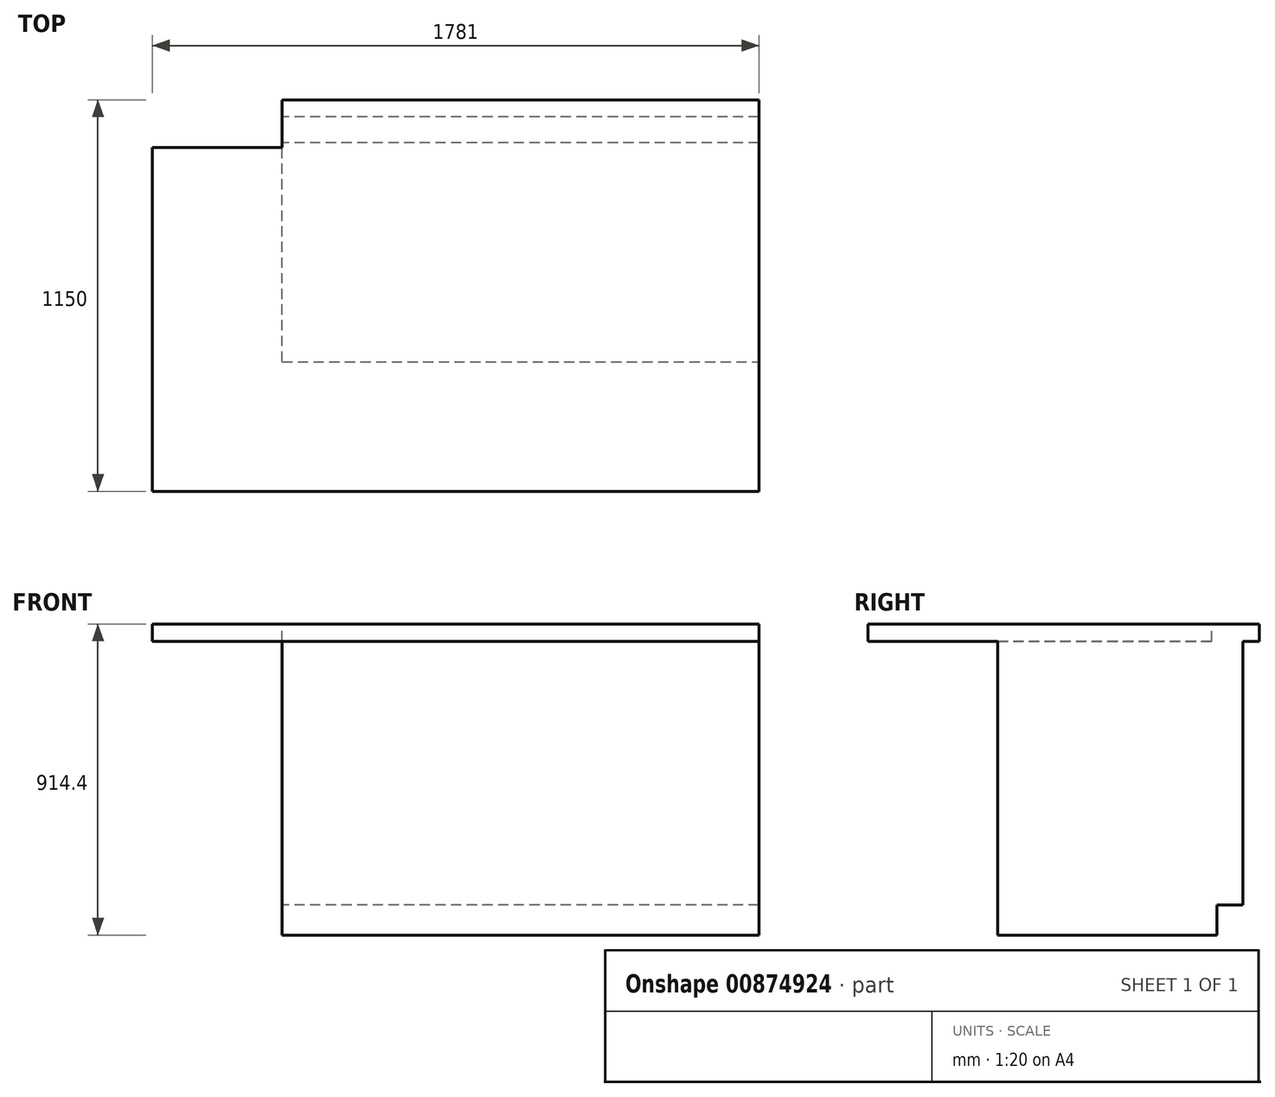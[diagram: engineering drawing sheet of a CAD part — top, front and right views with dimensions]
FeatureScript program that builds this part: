
annotation { "Feature Type Name" : "Feature", "Feature Type Description" : "" }
export const myFeature = defineFeature(function(context is Context, id is Id, definition is map)
    precondition{}
    {
        {
            var Q0;
            Q0=qCreatedBy(makeId("Top.planeOp"),FACE);
            var sketch = newSketch(context, id + "F0", { "sketchPlane" : qUnion([Q0])});
            skLineSegment(sketch, "E0.bottom", {"start": v(0, 0) * mm, "end": v(1400, 0) * mm});
            skLineSegment(sketch, "E0.top", {"start": v(0, 720) * mm, "end": v(1400, 720) * mm});
            skLineSegment(sketch, "E0.left", {"start": v(0, 0) * mm, "end": v(0, 720) * mm});
            skLineSegment(sketch, "E0.right", {"start": v(1400, 0) * mm, "end": v(1400, 720) * mm});
            skSolve(sketch);
        }
        {
            var Q0;
            Q0=makeQuery(id+"F0.imprint","IMPRINT",FACE,{"disambiguationData":[TD([[makeQuery(id+"F0.imprint","IMPRINT",EDGE,{"derivedFrom":sQuery(id+"F0.wireOp",EDGE,"E0.bottom")}),1.0]])]});
            extrude(context, id + "F1", {"entities" : qUnion([Q0]), "depth" : 863.6 * mm, "offsetDistance" : 25 * mm});
        }
        {
            var Q0;
            Q0=qCreatedBy(makeId("Right.planeOp"),FACE);
            var sketch = newSketch(context, id + "F2", { "sketchPlane" : qUnion([Q0])});
            skLineSegment(sketch, "E1.0", {"start": v(0, 0) * mm, "end": v(720, 0) * mm, "construction": true});
            skLineSegment(sketch, "E2.0", {"start": v(720, 863.6) * mm, "end": v(720, 0) * mm, "construction": true});
            skLineSegment(sketch, "E3.0", {"start": v(0, 863.6) * mm, "end": v(0, 0) * mm, "construction": true});
            skLineSegment(sketch, "E4.bottom", {"start": v(720, 0) * mm, "end": v(643.8, 0) * mm});
            skLineSegment(sketch, "E4.top", {"start": v(720, 88.9) * mm, "end": v(643.8, 88.9) * mm});
            skLineSegment(sketch, "E4.left", {"start": v(720, 0) * mm, "end": v(720, 88.9) * mm});
            skLineSegment(sketch, "E4.right", {"start": v(643.8, 0) * mm, "end": v(643.8, 88.9) * mm});
            skSolve(sketch);
        }
        {
            var Q0;
            Q0=qSketchRegion(id+"F2",true);
            extrude(context, id + "F3", {"entities" : qUnion([Q0]), "operationType" : NewBodyOperationType.REMOVE, "endBound" : BoundingType.THROUGH_ALL, "depth" : 25 * mm, "offsetDistance" : 25 * mm});
        }
        {
            var Q0;
            Q0=qCreatedBy(makeId("Right.planeOp"),FACE);
            var sketch = newSketch(context, id + "F4", { "sketchPlane" : qUnion([Q0])});
            skLineSegment(sketch, "E5.0", {"start": v(0, 863.6) * mm, "end": v(720, 863.6) * mm, "construction": true});
            skLineSegment(sketch, "E6.bottom", {"start": v(769, 863.6) * mm, "end": v(-381, 863.6) * mm});
            skLineSegment(sketch, "E6.top", {"start": v(769, 914.4) * mm, "end": v(-381, 914.4) * mm});
            skLineSegment(sketch, "E6.left", {"start": v(769, 863.6) * mm, "end": v(769, 914.4) * mm});
            skLineSegment(sketch, "E6.right", {"start": v(-381, 863.6) * mm, "end": v(-381, 914.4) * mm});
            skSolve(sketch);
        }
        {
            var Q0;
            Q0=makeQuery(id+"F4.imprint","IMPRINT",FACE,{"disambiguationData":[TD([[makeQuery(id+"F4.imprint","IMPRINT",EDGE,{"derivedFrom":sQuery(id+"F4.wireOp",EDGE,"E6.bottom")}),-1.0]])]});
            var Q1;
            Q1=makeQuery(id+"F1.opExtrude","SWEPT_FACE",FACE,{"disambiguationData":[OSD([sQuery(id+"F0.wireOp",EDGE,"E0.right")])]});
            extrude(context, id + "F5", {"entities" : qUnion([Q0]), "endBound" : BoundingType.UP_TO_SURFACE, "depth" : 25 * mm, "endBoundEntityFace" : qUnion([Q1]), "offsetDistance" : 25 * mm});
        }
        {
            var Q0;
            Q0=makeQuery(id+"F5.opExtrude","CAP_FACE",FACE,{"disambiguationData":[OSD([sQuery(id+"F4.wireOp",EDGE,"E6.bottom"),sQuery(id+"F4.wireOp",EDGE,"E6.top"),sQuery(id+"F4.wireOp",EDGE,"E6.left"),sQuery(id+"F4.wireOp",EDGE,"E6.right")])],"isStart":true});
            extrude(context, id + "F6", {"entities" : qUnion([Q0]), "operationType" : NewBodyOperationType.ADD, "depth" : 381 * mm, "offsetDistance" : 25 * mm});
        }
        {
            var Q0;
            {var subQ0=sQuery(id+"F4.wireOp",EDGE,"E6.top");Q0=makeQuery(id+"F6.boolean.opBoolean","MERGE",FACE,{"derivedFrom":[makeQuery(id+"F5.opExtrude","SWEPT_FACE",FACE,{"disambiguationData":[OSD([subQ0])]}),makeQuery(id+"F6.opExtrude","SWEPT_FACE",FACE,{"disambiguationData":[OSD([subQ0])]})]});}
            var sketch = newSketch(context, id + "F7", { "sketchPlane" : qUnion([Q0])});
            skPoint(sketch, "E7.0", {"position": v(-381, 769) * mm});
            skLineSegment(sketch, "E8.bottom", {"start": v(-381, 769) * mm, "end": v(0, 769) * mm});
            skLineSegment(sketch, "E8.top", {"start": v(-381, 629) * mm, "end": v(0, 629) * mm});
            skLineSegment(sketch, "E8.left", {"start": v(-381, 769) * mm, "end": v(-381, 629) * mm});
            skLineSegment(sketch, "E8.right", {"start": v(0, 769) * mm, "end": v(0, 629) * mm});
            skSolve(sketch);
        }
        {
            var Q0;
            Q0=qSketchRegion(id+"F7",true);
            var Q1;
            {var subQ0=sQuery(id+"F4.wireOp",EDGE,"E6.bottom");Q1=makeQuery(id+"F6.boolean.opBoolean","MERGE",FACE,{"derivedFrom":[makeQuery(id+"F5.opExtrude","SWEPT_FACE",FACE,{"disambiguationData":[OSD([subQ0])]}),makeQuery(id+"F6.opExtrude","SWEPT_FACE",FACE,{"disambiguationData":[OSD([subQ0])]})]});}
            extrude(context, id + "F8", {"entities" : qUnion([Q0]), "operationType" : NewBodyOperationType.REMOVE, "endBound" : BoundingType.UP_TO_SURFACE, "oppositeDirection" : true, "depth" : 25 * mm, "endBoundEntityFace" : qUnion([Q1]), "offsetDistance" : 25 * mm});
        }
    });
